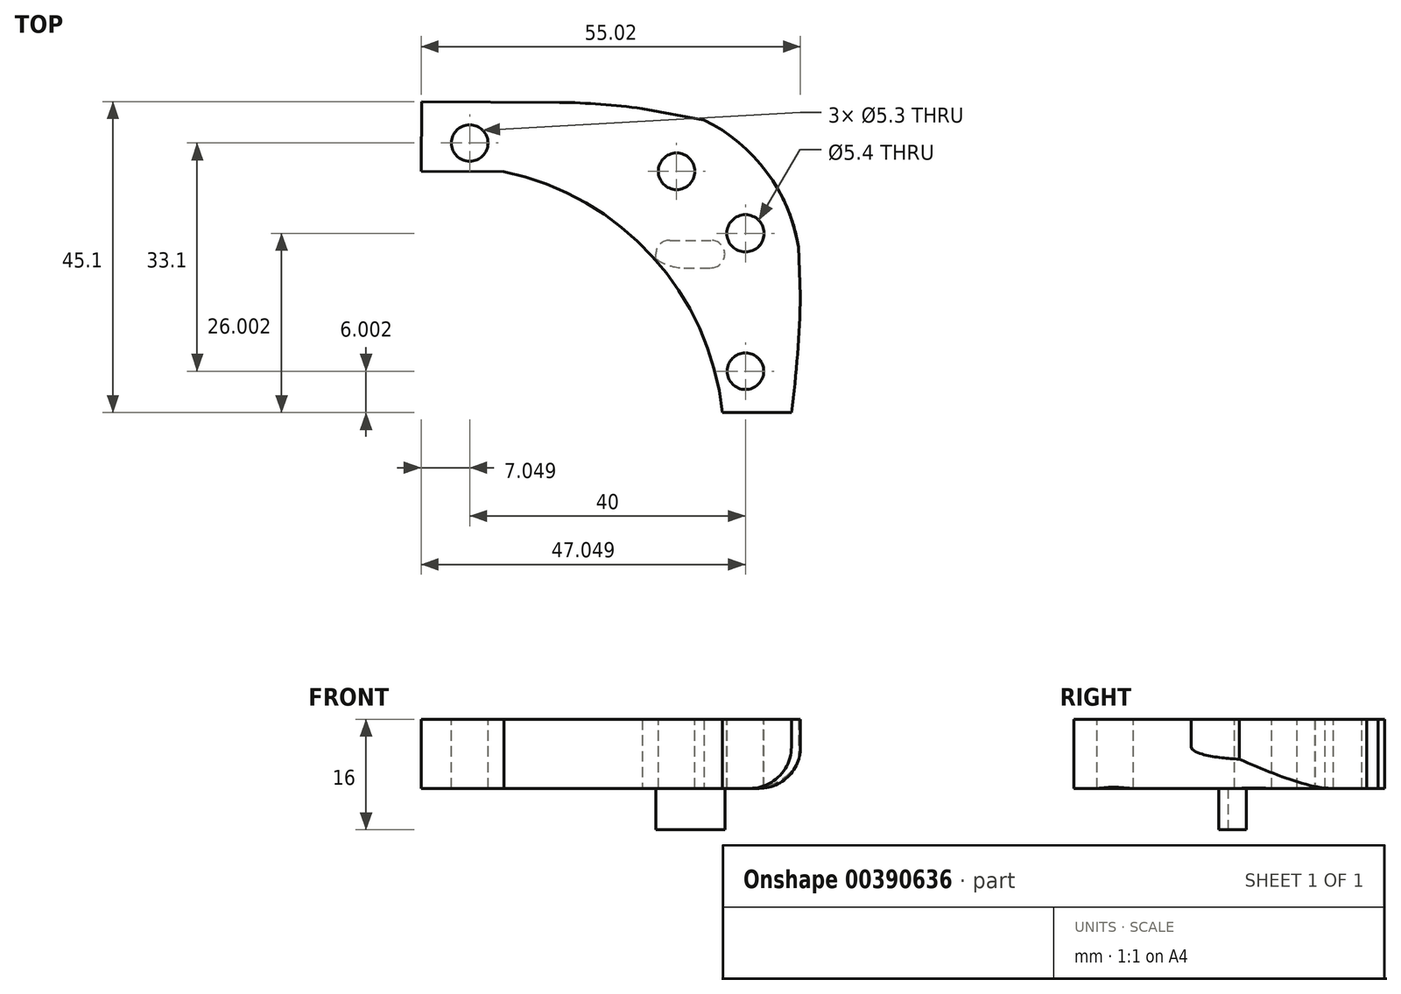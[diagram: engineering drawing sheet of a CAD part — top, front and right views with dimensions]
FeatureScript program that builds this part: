
annotation { "Feature Type Name" : "Feature", "Feature Type Description" : "" }
export const myFeature = defineFeature(function(context is Context, id is Id, definition is map)
    precondition{}
    {
        {
            var Q0;
            Q0=qCreatedBy(makeId("Top.planeOp"),FACE);
            var sketch = newSketch(context, id + "F0", { "sketchPlane" : qUnion([Q0])});
            skLineSegment(sketch, "E0", {"start": v(-53.66, -11.15) * mm, "end": v(-53.71, -21.25) * mm});
            skArc(sketch, "E1", {"start": v(-12.66, -13.8) * mm, "mid": v(-3.58, -21.36) * mm, "end": v(1.02, -32.25) * mm});
            skLineSegment(sketch, "E2", {"start": v(-53.66, -11.15) * mm, "end": v(-33.66, -11.25) * mm});
            skArc(sketch, "E3", {"start": v(-33.66, -11.25) * mm, "mid": v(-27.65, -11.52) * mm, "end": v(-21.66, -12.15) * mm});
            skLineSegment(sketch, "E4", {"start": v(-21.66, -12.15) * mm, "end": v(-12.66, -13.8) * mm});
            skPoint(sketch, "E5.orphan", {"position": v(1.34, -36.25) * mm});
            skArc(sketch, "E6", {"start": v(0, -56.25) * mm, "mid": v(0.9, -47.77) * mm, "end": v(1.3, -39.25) * mm});
            skLineSegment(sketch, "E7", {"start": v(0, -56.25) * mm, "end": v(-10, -56.25) * mm});
            skLineSegment(sketch, "E8", {"start": v(-53.71, -21.25) * mm, "end": v(-41.71, -21.3) * mm});
            skArc(sketch, "E9", {"start": v(-10, -56.25) * mm, "mid": v(-20.16, -33.6) * mm, "end": v(-41.71, -21.3) * mm});
            skLineSegment(sketch, "E10", {"start": v(1.02, -32.25) * mm, "end": v(1.3, -39.25) * mm});
            skSolve(sketch);
        }
        {
            var Q0;
            Q0=qSketchRegion(id+"F0",true);
            extrude(context, id + "F1", {"entities" : qUnion([Q0]), "depth" : 10 * mm});
        }
        {
            var Q0;
            Q0=makeQuery(id+"F1.opExtrude","CAP_FACE",FACE,{"disambiguationData":[OSD([sQuery(id+"F0.wireOp",EDGE,"sl27yMI0-AFCf-Kcrl-0bmQ-pZ9rT9zFnCGi"),sQuery(id+"F0.wireOp",EDGE,"BDBsffxZ-tEOx-Hil9-iUUA-GEFrlKPdEFfM"),sQuery(id+"F0.wireOp",EDGE,"E0"),sQuery(id+"F0.wireOp",EDGE,"FjBfGWs7-kI8q-3lPp-M7p8-NHLP12ySko6t"),sQuery(id+"F0.wireOp",EDGE,"xpgikVl3-DIja-vaeT-NMQl-5fUiDFNzWjIU"),sQuery(id+"F0.wireOp",EDGE,"E1"),sQuery(id+"F0.wireOp",EDGE,"15a26400-cb63-4f5f-8ce6-d631993ec03b")])],"isStart":false});
            var sketch = newSketch(context, id + "F2", { "sketchPlane" : qUnion([Q0])});
            skCircle(sketch, "E11", {"center": v(-46.66, -17.15) * mm, "radius": 2.65 * mm});
            skCircle(sketch, "E12", {"center": v(-16.66, -21.25) * mm, "radius": 2.65 * mm});
            skCircle(sketch, "E13", {"center": v(-6.66, -50.25) * mm, "radius": 2.65 * mm});
            skCircle(sketch, "E14", {"center": v(-6.66, -30.25) * mm, "radius": 2.7 * mm});
            skSolve(sketch);
        }
        {
            var Q0;
            Q0=qSketchRegion(id+"F2",true);
            extrude(context, id + "F3", {"entities" : qUnion([Q0]), "operationType" : NewBodyOperationType.REMOVE, "endBound" : BoundingType.THROUGH_ALL, "oppositeDirection" : true, "depth" : 25 * mm});
        }
        {
            var Q0;
            Q0=makeQuery(id+"F1.opExtrude","CAP_EDGE",EDGE,{"disambiguationData":[OSD([sQuery(id+"F0.wireOp",EDGE,"E6")])],"isStart":true});
            fillet(context, id + "F4", {"entities" : qUnion([Q0]), "radius" : 6 * mm, "allowEdgeOverflow" : false});
        }
        {
            var Q0;
            Q0=makeQuery(id+"F0.imprint","IMPRINT",FACE,{"disambiguationData":[TD([[makeQuery(id+"F0.imprint","IMPRINT",EDGE,{"derivedFrom":sQuery(id+"F0.wireOp",EDGE,"E0")}),1.0]])]});
            var sketch = newSketch(context, id + "F5", { "sketchPlane" : qUnion([Q0])});
            skLineSegment(sketch, "E15.bottom", {"start": v(-19.66, -35.25) * mm, "end": v(-9.66, -35.25) * mm});
            skLineSegment(sketch, "E15.top", {"start": v(-19.66, -31.25) * mm, "end": v(-9.66, -31.25) * mm});
            skLineSegment(sketch, "E15.left", {"start": v(-19.66, -35.25) * mm, "end": v(-19.66, -31.25) * mm});
            skLineSegment(sketch, "E15.right", {"start": v(-9.66, -35.25) * mm, "end": v(-9.66, -31.25) * mm});
            skSolve(sketch);
        }
        {
            var Q0;
            {var subQ2=sQuery(id+"F5.wireOp",EDGE,"E15.top");Q0=makeQuery(id+"F5.imprint","IMPRINT",FACE,{"disambiguationData":[TD([[makeQuery(id+"F5.imprint","IMPRINT",EDGE,{"derivedFrom":subQ2}),-1.0]])]});}
            extrude(context, id + "F6", {"entities" : qUnion([Q0]), "operationType" : NewBodyOperationType.ADD, "oppositeDirection" : true, "depth" : 6 * mm});
        }
        {
            var Q0;
            Q0=makeQuery(id+"F6.opExtrude","SWEPT_EDGE",EDGE,{"disambiguationData":[OSD([sQuery(id+"F5.wireOp",EDGE,"E15.top"),sQuery(id+"F5.wireOp",EDGE,"E15.left")])]});
            var Q1;
            Q1=makeQuery(id+"F6.opExtrude","SWEPT_EDGE",EDGE,{"disambiguationData":[OSD([sQuery(id+"F5.wireOp",EDGE,"E15.top"),sQuery(id+"F5.wireOp",EDGE,"E15.right")])]});
            var Q2;
            Q2=makeQuery(id+"F6.opExtrude","SWEPT_EDGE",EDGE,{"disambiguationData":[OSD([sQuery(id+"F5.wireOp",EDGE,"E15.bottom"),sQuery(id+"F5.wireOp",EDGE,"E15.right")])]});
            fillet(context, id + "F7", {"entities" : qUnion([Q0, Q1, Q2]), "radius" : 2 * mm, "tangentPropagation" : true, "allowEdgeOverflow" : false});
        }
        {
            var Q0;
            Q0=makeQuery(id+"F6.opExtrude","SWEPT_EDGE",EDGE,{"disambiguationData":[OSD([sQuery(id+"F0.wireOp",EDGE,"E9"),sQuery(id+"F5.wireOp",EDGE,"E15.bottom")])]});
            fillet(context, id + "F8", {"entities" : qUnion([Q0]), "radius" : 7 * mm, "tangentPropagation" : true, "allowEdgeOverflow" : false});
        }
    });
